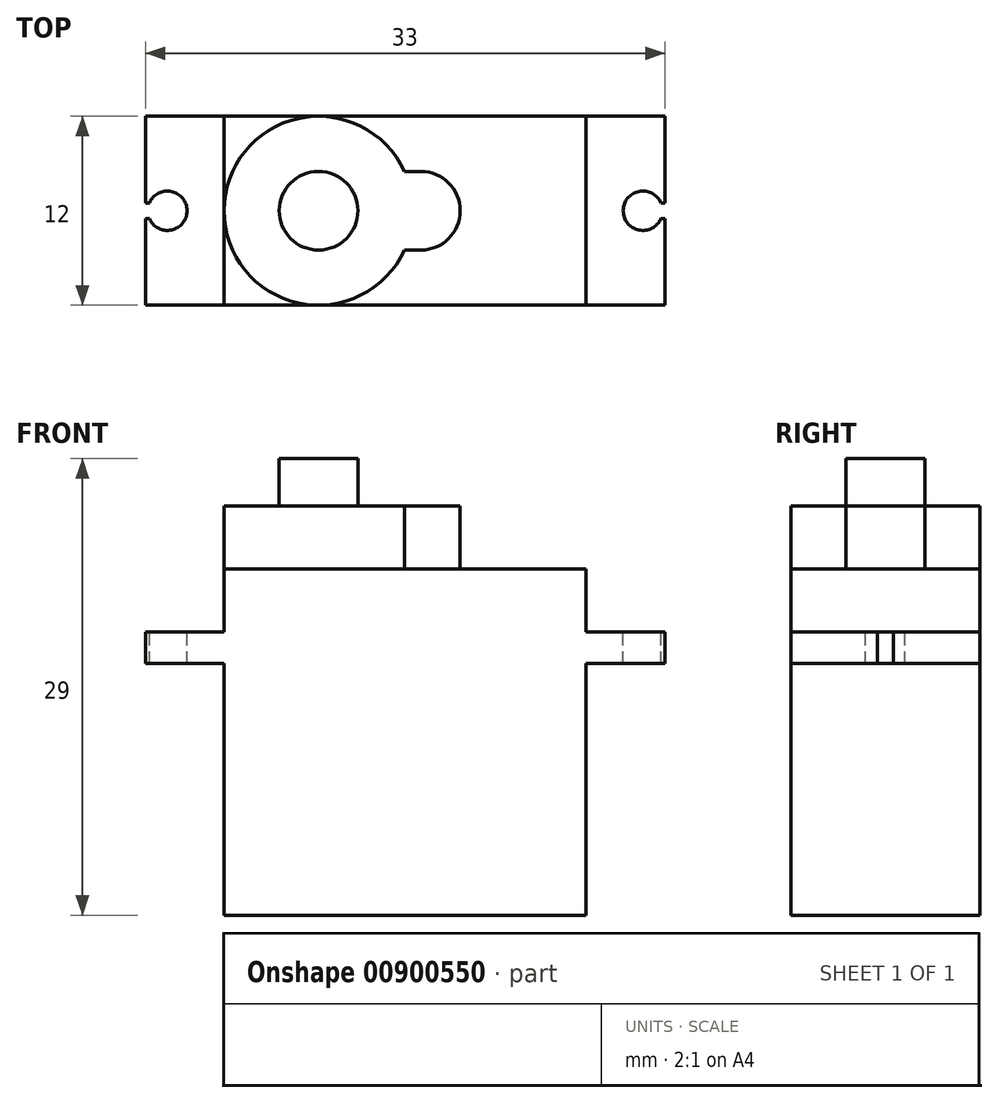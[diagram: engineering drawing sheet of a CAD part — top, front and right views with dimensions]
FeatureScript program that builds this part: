
annotation { "Feature Type Name" : "Feature", "Feature Type Description" : "" }
export const myFeature = defineFeature(function(context is Context, id is Id, definition is map)
    precondition{}
    {
        {
            var Q0;
            Q0=qCreatedBy(makeId("Front.planeOp"),FACE);
            var sketch = newSketch(context, id + "F0", { "sketchPlane" : qUnion([Q0])});
            skLineSegment(sketch, "E0.bottom", {"start": v(-11.5, 0) * mm, "end": v(11.5, 0) * mm});
            skLineSegment(sketch, "E0.top", {"start": v(-11.5, 22) * mm, "end": v(11.5, 22) * mm});
            skLineSegment(sketch, "E0.left", {"start": v(-11.5, 0) * mm, "end": v(-11.5, 22) * mm});
            skLineSegment(sketch, "E0.right", {"start": v(11.5, 0) * mm, "end": v(11.5, 22) * mm});
            skSolve(sketch);
        }
        {
            var Q0;
            Q0 = qSketchRegion(id + "F0", true);
            extrude(context, id + "F1", {"entities" : qUnion([Q0]), "endBound" : BoundingType.SYMMETRIC, "depth" : 12 * mm, "offsetDistance" : 25 * mm});
        }
        {
            var Q0;
            Q0=makeQuery(id+"F1.opExtrude","CAP_FACE",FACE,{"disambiguationData":[OSD([sQuery(id+"F0.wireOp",EDGE,"E0.bottom"),sQuery(id+"F0.wireOp",EDGE,"E0.top"),sQuery(id+"F0.wireOp",EDGE,"E0.left"),sQuery(id+"F0.wireOp",EDGE,"E0.right")])],"isStart":false});
            var sketch = newSketch(context, id + "F2", { "sketchPlane" : qUnion([Q0])});
            skLineSegment(sketch, "E1.bottom", {"start": v(-16.5, 18) * mm, "end": v(16.5, 18) * mm});
            skLineSegment(sketch, "E1.top", {"start": v(-16.5, 16) * mm, "end": v(16.5, 16) * mm});
            skLineSegment(sketch, "E1.left", {"start": v(-16.5, 18) * mm, "end": v(-16.5, 16) * mm});
            skLineSegment(sketch, "E1.right", {"start": v(16.5, 18) * mm, "end": v(16.5, 16) * mm});
            skSolve(sketch);
        }
        {
            var Q0;
            Q0 = qSketchRegion(id + "F2", true);
            extrude(context, id + "F3", {"entities" : qUnion([Q0]), "operationType" : NewBodyOperationType.ADD, "oppositeDirection" : true, "depth" : 12 * mm, "offsetDistance" : 25 * mm});
        }
        {
            var Q0;
            Q0=makeQuery(id+"F1.opExtrude","SWEPT_FACE",FACE,{"disambiguationData":[OSD([sQuery(id+"F0.wireOp",EDGE,"E0.top")])]});
            var sketch = newSketch(context, id + "F4", { "sketchPlane" : qUnion([Q0])});
            skCircle(sketch, "E2", {"center": v(-5.5, 0) * mm, "radius": 6 * mm});
            skSolve(sketch);
        }
        {
            var Q0;
            Q0 = qSketchRegion(id + "F4", true);
            extrude(context, id + "F5", {"entities" : qUnion([Q0]), "operationType" : NewBodyOperationType.ADD, "depth" : 4 * mm, "offsetDistance" : 25 * mm});
        }
        {
            var Q0;
            {var subQ0=sQuery(id+"F0.wireOp",EDGE,"E0.right");var subQ1=sQuery(id+"F0.wireOp",EDGE,"E0.top");var subQ2=makeQuery(id+"F1.opExtrude","SWEPT_FACE",FACE,{"disambiguationData":[OSD([subQ1])]});var subQ3=sQuery(id+"F2.wireOp",EDGE,"E1.right");var subQ4=sQuery(id+"F2.wireOp",EDGE,"E1.left");var subQ5=sQuery(id+"F2.wireOp",EDGE,"E1.top");var subQ6=sQuery(id+"F2.wireOp",EDGE,"E1.bottom");var subQ7=sQuery(id+"F0.wireOp",EDGE,"E0.left");var subQ8=sQuery(id+"F0.wireOp",EDGE,"E0.bottom");Q0=makeQuery(id+"F5.boolean.opBoolean","SPLIT",FACE,{"disambiguationData":[TD([makeQuery(id+"F1.opExtrude","CAP_FACE",FACE,{"disambiguationData":[OSD([subQ8,subQ1,subQ7,subQ0])],"isStart":true}),makeQuery(id+"F1.opExtrude","CAP_FACE",FACE,{"disambiguationData":[OSD([subQ8,subQ1,subQ7,subQ0])],"isStart":false}),subQ2,makeQuery(id+"F1.opExtrude","SWEPT_FACE",FACE,{"disambiguationData":[OSD([subQ0])]}),makeQuery(id+"F3.opExtrude","CAP_FACE",FACE,{"disambiguationData":[OSD([subQ6,subQ5,subQ4,subQ3])],"isStart":true}),makeQuery(id+"F3.opExtrude","CAP_FACE",FACE,{"disambiguationData":[OSD([subQ6,subQ5,subQ4,subQ3])],"isStart":false}),makeQuery(id+"F5.opExtrude","SWEPT_FACE",FACE,{"disambiguationData":[OSD([sQuery(id+"F4.wireOp",EDGE,"E2")])]})])],"derivedFrom":subQ2});}
            var sketch = newSketch(context, id + "F6", { "sketchPlane" : qUnion([Q0])});
            skArc(sketch, "E3", {"start": v(1, -2.5) * mm, "mid": v(3.5, 0) * mm, "end": v(1, 2.5) * mm});
            skLineSegment(sketch, "E4", {"start": v(1, 2.5) * mm, "end": v(-2, 2.5) * mm});
            skLineSegment(sketch, "E5", {"start": v(1, -2.5) * mm, "end": v(-2, -2.5) * mm});
            skLineSegment(sketch, "E6", {"start": v(-2, -2.5) * mm, "end": v(-2, 2.5) * mm});
            skSolve(sketch);
        }
        {
            var Q0;
            Q0 = qSketchRegion(id + "F6", true);
            extrude(context, id + "F7", {"entities" : qUnion([Q0]), "operationType" : NewBodyOperationType.ADD, "depth" : 4 * mm, "offsetDistance" : 25 * mm});
        }
        {
            var Q0;
            Q0=makeQuery(id+"F7.boolean.opBoolean","MERGE",FACE,{"derivedFrom":[makeQuery(id+"F5.opExtrude","CAP_FACE",FACE,{"disambiguationData":[OSD([sQuery(id+"F4.wireOp",EDGE,"E2")])],"isStart":false}),makeQuery(id+"F7.opExtrude","CAP_FACE",FACE,{"disambiguationData":[OSD([sQuery(id+"F6.wireOp",EDGE,"E3"),sQuery(id+"F6.wireOp",EDGE,"E4"),sQuery(id+"F6.wireOp",EDGE,"E5"),sQuery(id+"F6.wireOp",EDGE,"E6")])],"isStart":false})]});
            var sketch = newSketch(context, id + "F8", { "sketchPlane" : qUnion([Q0])});
            skCircle(sketch, "E7", {"center": v(-5.5, 0) * mm, "radius": 2.5 * mm});
            skSolve(sketch);
        }
        {
            var Q0;
            Q0 = qSketchRegion(id + "F8", true);
            extrude(context, id + "F9", {"entities" : qUnion([Q0]), "operationType" : NewBodyOperationType.ADD, "depth" : 3 * mm, "offsetDistance" : 25 * mm});
        }
        {
            var Q0;
            {var subQ3=sQuery(id+"F2.wireOp",EDGE,"E1.bottom");var subQ4=sQuery(id+"F0.wireOp",EDGE,"E0.right");Q0=makeQuery(id+"F3.boolean.opBoolean","SPLIT",FACE,{"disambiguationData":[TD([makeQuery(id+"F1.opExtrude","SWEPT_FACE",FACE,{"disambiguationData":[OSD([subQ4])]})])],"derivedFrom":makeQuery(id+"F3.opExtrude","SWEPT_FACE",FACE,{"disambiguationData":[OSD([subQ3])]})});}
            var sketch = newSketch(context, id + "F10", { "sketchPlane" : qUnion([Q0])});
            skArc(sketch, "E8", {"start": v(16.25, 0.5) * mm, "mid": v(13.85, 0) * mm, "end": v(16.25, -0.5) * mm});
            skLineSegment(sketch, "E9.bottom", {"start": v(16.25, 0.5) * mm, "end": v(16.75, 0.5) * mm});
            skLineSegment(sketch, "E9.top", {"start": v(16.25, -0.5) * mm, "end": v(16.75, -0.5) * mm});
            skLineSegment(sketch, "E9.right", {"start": v(16.75, 0.5) * mm, "end": v(16.75, -0.5) * mm});
            skSolve(sketch);
        }
        {
            var Q0;
            Q0 = qSketchRegion(id + "F10", true);
            extrude(context, id + "F11", {"entities" : qUnion([Q0]), "operationType" : NewBodyOperationType.REMOVE, "endBound" : BoundingType.THROUGH_ALL, "oppositeDirection" : true, "depth" : 25 * mm, "offsetDistance" : 25 * mm});
        }
        {
            var Q0;
            {var subQ3=sQuery(id+"F2.wireOp",EDGE,"E1.bottom");var subQ5=sQuery(id+"F0.wireOp",EDGE,"E0.left");Q0=makeQuery(id+"F3.boolean.opBoolean","SPLIT",FACE,{"disambiguationData":[TD([makeQuery(id+"F1.opExtrude","SWEPT_FACE",FACE,{"disambiguationData":[OSD([subQ5])]})])],"derivedFrom":makeQuery(id+"F3.opExtrude","SWEPT_FACE",FACE,{"disambiguationData":[OSD([subQ3])]})});}
            var sketch = newSketch(context, id + "F12", { "sketchPlane" : qUnion([Q0])});
            skArc(sketch, "E10", {"start": v(-16.25, -0.5) * mm, "mid": v(-13.85, 0) * mm, "end": v(-16.25, 0.5) * mm});
            skLineSegment(sketch, "E11.bottom", {"start": v(-16.93, 0.5) * mm, "end": v(-16.25, 0.5) * mm});
            skLineSegment(sketch, "E11.top", {"start": v(-16.93, -0.5) * mm, "end": v(-16.25, -0.5) * mm});
            skLineSegment(sketch, "E11.left", {"start": v(-16.93, 0.5) * mm, "end": v(-16.93, -0.5) * mm});
            skSolve(sketch);
        }
        {
            var Q0;
            Q0 = qSketchRegion(id + "F12", true);
            extrude(context, id + "F13", {"entities" : qUnion([Q0]), "operationType" : NewBodyOperationType.REMOVE, "endBound" : BoundingType.THROUGH_ALL, "oppositeDirection" : true, "depth" : 25 * mm, "offsetDistance" : 25 * mm});
        }
    });
